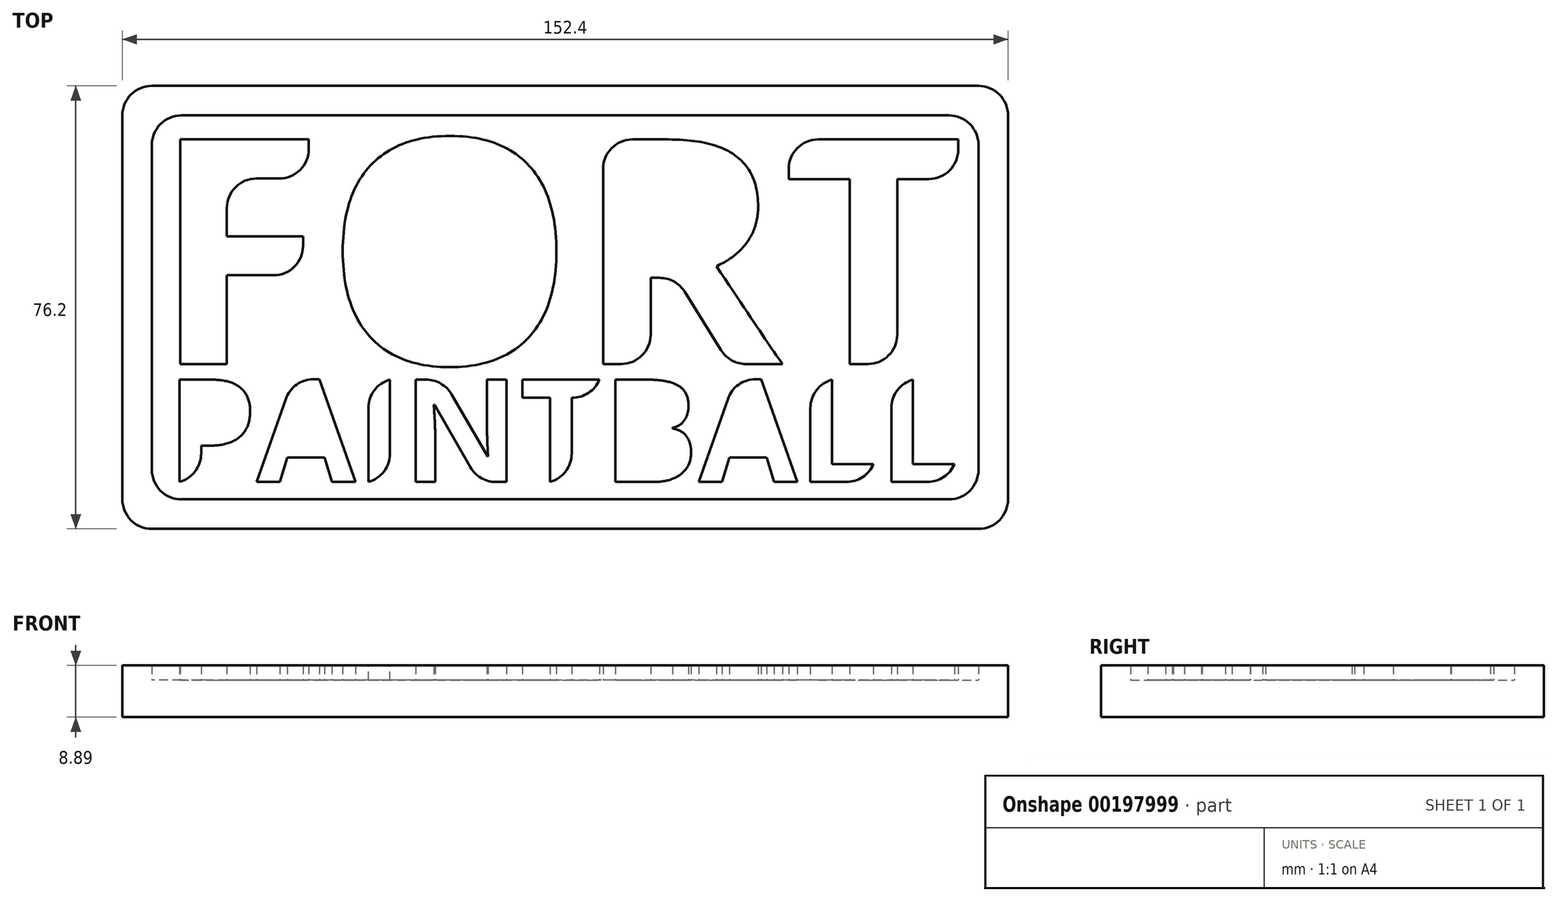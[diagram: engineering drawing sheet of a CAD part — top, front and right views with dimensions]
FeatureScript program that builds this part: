
annotation { "Feature Type Name" : "Feature", "Feature Type Description" : "" }
export const myFeature = defineFeature(function(context is Context, id is Id, definition is map)
    precondition{}
    {
        {
            var Q0;
            Q0=qCreatedBy(makeId("Top.planeOp"),FACE);
            var sketch = newSketch(context, id + "F0", { "sketchPlane" : qUnion([Q0])});
            skLineSegment(sketch, "E0.bottom", {"start": v(76.2, -38.1) * mm, "end": v(-76.2, -38.1) * mm});
            skLineSegment(sketch, "E0.top", {"start": v(76.2, 38.1) * mm, "end": v(-76.2, 38.1) * mm});
            skLineSegment(sketch, "E0.left", {"start": v(76.2, -38.1) * mm, "end": v(76.2, 38.1) * mm});
            skLineSegment(sketch, "E0.right", {"start": v(-76.2, -38.1) * mm, "end": v(-76.2, 38.1) * mm});
            skPoint(sketch, "E0.middle", {"position": v(0, 0) * mm});
            skText(sketch, "E1", { "text": "FORT", "fontName": "OpenSans-Bold.ttf"});
            skLineSegment(sketch, "E2.0", {"start": v(71.12, 33.02) * mm, "end": v(-71.12, 33.02) * mm});
            skLineSegment(sketch, "E2.1", {"start": v(71.12, -33.02) * mm, "end": v(71.12, 33.02) * mm});
            skLineSegment(sketch, "E2.2", {"start": v(71.12, -33.02) * mm, "end": v(-71.12, -33.02) * mm});
            skLineSegment(sketch, "E2.3", {"start": v(-71.12, -33.02) * mm, "end": v(-71.12, 33.02) * mm});
            skText(sketch, "E3", { "text": "PAINTBALL", "fontName": "OpenSans-Bold.ttf"});
            const initialGuessF0  = {"E1": [-0.07112, -0.00975, 1, 0, 0.03896], "E3": [-0.06858, -0.03004, 1, 0, 0.01775]};
            skSetInitialGuess(sketch, initialGuessF0);
            skSolve(sketch);
        }
        {
            var Q0;
            Q0=makeQuery(id+"F0.imprint","IMPRINT",FACE,{"disambiguationData":[TD([[makeQuery(id+"F0.imprint","IMPRINT",EDGE,{"derivedFrom":sQuery(id+"F0.wireOp",EDGE,"E1.sketch_text.stroke-0")}),1.0]])]});
            extrude(context, id + "F1", {"entities" : qUnion([Q0]), "depth" : 6.35 * mm});
        }
        {
            var Q0;
            Q0=makeQuery(id+"F0.imprint","IMPRINT",FACE,{"disambiguationData":[TD([[makeQuery(id+"F0.imprint","IMPRINT",EDGE,{"derivedFrom":sQuery(id+"F0.wireOp",EDGE,"E3.sketch_text.stroke-79")}),-1.0]])]});
            var Q1;
            Q1=makeQuery(id+"F0.imprint","IMPRINT",FACE,{"disambiguationData":[TD([[makeQuery(id+"F0.imprint","IMPRINT",EDGE,{"derivedFrom":sQuery(id+"F0.wireOp",EDGE,"E3.sketch_text.stroke-87")}),1.0]])]});
            var Q2;
            Q2=makeQuery(id+"F0.imprint","IMPRINT",FACE,{"disambiguationData":[TD([[makeQuery(id+"F0.imprint","IMPRINT",EDGE,{"derivedFrom":sQuery(id+"F0.wireOp",EDGE,"E3.sketch_text.stroke-91")}),-1.0]])]});
            var Q3;
            Q3=makeQuery(id+"F0.imprint","IMPRINT",FACE,{"disambiguationData":[TD([[makeQuery(id+"F0.imprint","IMPRINT",EDGE,{"derivedFrom":sQuery(id+"F0.wireOp",EDGE,"E3.sketch_text.stroke-97")}),-1.0]])]});
            var Q4;
            Q4=makeQuery(id+"F0.imprint","IMPRINT",FACE,{"disambiguationData":[TD([[makeQuery(id+"F0.imprint","IMPRINT",EDGE,{"derivedFrom":sQuery(id+"F0.wireOp",EDGE,"E1.sketch_text.stroke-43")}),-1.0]])]});
            var Q5;
            Q5=makeQuery(id+"F0.imprint","IMPRINT",FACE,{"disambiguationData":[TD([[makeQuery(id+"F0.imprint","IMPRINT",EDGE,{"derivedFrom":sQuery(id+"F0.wireOp",EDGE,"E1.sketch_text.stroke-24")}),1.0]])]});
            var Q6;
            Q6=makeQuery(id+"F0.imprint","IMPRINT",FACE,{"disambiguationData":[TD([[makeQuery(id+"F0.imprint","IMPRINT",EDGE,{"derivedFrom":sQuery(id+"F0.wireOp",EDGE,"E1.sketch_text.stroke-24")}),-1.0]])]});
            var Q7;
            Q7=makeQuery(id+"F0.imprint","IMPRINT",FACE,{"disambiguationData":[TD([[makeQuery(id+"F0.imprint","IMPRINT",EDGE,{"derivedFrom":sQuery(id+"F0.wireOp",EDGE,"E1.sketch_text.stroke-10")}),-1.0]])]});
            var Q8;
            Q8=makeQuery(id+"F0.imprint","IMPRINT",FACE,{"disambiguationData":[TD([[makeQuery(id+"F0.imprint","IMPRINT",EDGE,{"derivedFrom":sQuery(id+"F0.wireOp",EDGE,"E1.sketch_text.stroke-18")}),1.0]])]});
            var Q9;
            Q9=makeQuery(id+"F0.imprint","IMPRINT",FACE,{"disambiguationData":[TD([[makeQuery(id+"F0.imprint","IMPRINT",EDGE,{"derivedFrom":sQuery(id+"F0.wireOp",EDGE,"E1.sketch_text.stroke-0")}),-1.0]])]});
            var Q10;
            Q10=makeQuery(id+"F0.imprint","IMPRINT",FACE,{"disambiguationData":[TD([[makeQuery(id+"F0.imprint","IMPRINT",EDGE,{"derivedFrom":sQuery(id+"F0.wireOp",EDGE,"E3.sketch_text.stroke-0")}),1.0]])]});
            var Q11;
            Q11=makeQuery(id+"F0.imprint","IMPRINT",FACE,{"disambiguationData":[TD([[makeQuery(id+"F0.imprint","IMPRINT",EDGE,{"derivedFrom":sQuery(id+"F0.wireOp",EDGE,"E3.sketch_text.stroke-0")}),-1.0]])]});
            var Q12;
            Q12=makeQuery(id+"F0.imprint","IMPRINT",FACE,{"disambiguationData":[TD([[makeQuery(id+"F0.imprint","IMPRINT",EDGE,{"derivedFrom":sQuery(id+"F0.wireOp",EDGE,"E3.sketch_text.stroke-16")}),-1.0]])]});
            var Q13;
            Q13=makeQuery(id+"F0.imprint","IMPRINT",FACE,{"disambiguationData":[TD([[makeQuery(id+"F0.imprint","IMPRINT",EDGE,{"derivedFrom":sQuery(id+"F0.wireOp",EDGE,"E3.sketch_text.stroke-24")}),1.0]])]});
            var Q14;
            Q14=makeQuery(id+"F0.imprint","IMPRINT",FACE,{"disambiguationData":[TD([[makeQuery(id+"F0.imprint","IMPRINT",EDGE,{"derivedFrom":sQuery(id+"F0.wireOp",EDGE,"E3.sketch_text.stroke-28")}),-1.0]])]});
            var Q15;
            Q15=makeQuery(id+"F0.imprint","IMPRINT",FACE,{"disambiguationData":[TD([[makeQuery(id+"F0.imprint","IMPRINT",EDGE,{"derivedFrom":sQuery(id+"F0.wireOp",EDGE,"E3.sketch_text.stroke-32")}),-1.0]])]});
            var Q16;
            Q16=makeQuery(id+"F0.imprint","IMPRINT",FACE,{"disambiguationData":[TD([[makeQuery(id+"F0.imprint","IMPRINT",EDGE,{"derivedFrom":sQuery(id+"F0.wireOp",EDGE,"E3.sketch_text.stroke-46")}),-1.0]])]});
            var Q17;
            Q17=makeQuery(id+"F0.imprint","IMPRINT",FACE,{"disambiguationData":[TD([[makeQuery(id+"F0.imprint","IMPRINT",EDGE,{"derivedFrom":sQuery(id+"F0.wireOp",EDGE,"E3.sketch_text.stroke-66")}),1.0]])]});
            var Q18;
            Q18=makeQuery(id+"F0.imprint","IMPRINT",FACE,{"disambiguationData":[TD([[makeQuery(id+"F0.imprint","IMPRINT",EDGE,{"derivedFrom":sQuery(id+"F0.wireOp",EDGE,"E3.sketch_text.stroke-54")}),-1.0]])]});
            var Q19;
            Q19=makeQuery(id+"F0.imprint","IMPRINT",FACE,{"disambiguationData":[TD([[makeQuery(id+"F0.imprint","IMPRINT",EDGE,{"derivedFrom":sQuery(id+"F0.wireOp",EDGE,"E3.sketch_text.stroke-73")}),1.0]])]});
            var Q20;
            Q20=makeQuery(id+"F0.imprint","IMPRINT",FACE,{"disambiguationData":[TD([[makeQuery(id+"F0.imprint","IMPRINT",EDGE,{"derivedFrom":sQuery(id+"F0.wireOp",EDGE,"E0.bottom")}),-1.0]])]});
            extrude(context, id + "F2", {"entities" : qUnion([Q0, Q1, Q2, Q3, Q4, Q5, Q6, Q7, Q8, Q9, Q10, Q11, Q12, Q13, Q14, Q15, Q16, Q17, Q18, Q19, Q20]), "operationType" : NewBodyOperationType.ADD, "depth" : 8.9 * mm});
        }
        {
            var Q0;
            Q0=makeQuery(id+"F2.opExtrude","SWEPT_EDGE",EDGE,{"disambiguationData":[OSD([sQuery(id+"F0.wireOp",EDGE,"E1.sketch_text.stroke-43"),sQuery(id+"F0.wireOp",EDGE,"E1.sketch_text.stroke-50")])]});
            var Q1;
            Q1=makeQuery(id+"F2.opExtrude","SWEPT_EDGE",EDGE,{"disambiguationData":[OSD([sQuery(id+"F0.wireOp",EDGE,"E1.sketch_text.stroke-46"),sQuery(id+"F0.wireOp",EDGE,"E1.sketch_text.stroke-47")])]});
            var Q2;
            Q2=makeQuery(id+"F2.opExtrude","SWEPT_EDGE",EDGE,{"disambiguationData":[OSD([sQuery(id+"F0.wireOp",EDGE,"E1.sketch_text.stroke-48"),sQuery(id+"F0.wireOp",EDGE,"E1.sketch_text.stroke-49")])]});
            var Q3;
            Q3=makeQuery(id+"F2.opExtrude","SWEPT_EDGE",EDGE,{"disambiguationData":[OSD([sQuery(id+"F0.wireOp",EDGE,"E1.sketch_text.stroke-33"),sQuery(id+"F0.wireOp",EDGE,"E1.sketch_text.stroke-34")])]});
            var Q4;
            Q4=makeQuery(id+"F2.opExtrude","SWEPT_EDGE",EDGE,{"disambiguationData":[OSD([sQuery(id+"F0.wireOp",EDGE,"E1.sketch_text.stroke-40"),sQuery(id+"F0.wireOp",EDGE,"E1.sketch_text.stroke-41")])]});
            var Q5;
            Q5=makeQuery(id+"F2.opExtrude","SWEPT_EDGE",EDGE,{"disambiguationData":[OSD([sQuery(id+"F0.wireOp",EDGE,"E1.sketch_text.stroke-31"),sQuery(id+"F0.wireOp",EDGE,"E1.sketch_text.stroke-32")])]});
            var Q6;
            Q6=makeQuery(id+"F2.opExtrude","SWEPT_EDGE",EDGE,{"disambiguationData":[OSD([sQuery(id+"F0.wireOp",EDGE,"E1.sketch_text.stroke-3"),sQuery(id+"F0.wireOp",EDGE,"E1.sketch_text.stroke-4")])]});
            var Q7;
            Q7=makeQuery(id+"F2.opExtrude","SWEPT_EDGE",EDGE,{"disambiguationData":[OSD([sQuery(id+"F0.wireOp",EDGE,"E1.sketch_text.stroke-7"),sQuery(id+"F0.wireOp",EDGE,"E1.sketch_text.stroke-8")])]});
            var Q8;
            Q8=makeQuery(id+"F2.opExtrude","SWEPT_EDGE",EDGE,{"disambiguationData":[OSD([sQuery(id+"F0.wireOp",EDGE,"E3.sketch_text.stroke-20"),sQuery(id+"F0.wireOp",EDGE,"E3.sketch_text.stroke-21")])]});
            var Q9;
            Q9=makeQuery(id+"F2.opExtrude","SWEPT_EDGE",EDGE,{"disambiguationData":[OSD([sQuery(id+"F0.wireOp",EDGE,"E3.sketch_text.stroke-28"),sQuery(id+"F0.wireOp",EDGE,"E3.sketch_text.stroke-29")])]});
            var Q10;
            Q10=makeQuery(id+"F2.opExtrude","SWEPT_EDGE",EDGE,{"disambiguationData":[OSD([sQuery(id+"F0.wireOp",EDGE,"E3.sketch_text.stroke-30"),sQuery(id+"F0.wireOp",EDGE,"E3.sketch_text.stroke-31")])]});
            var Q11;
            Q11=makeQuery(id+"F2.opExtrude","SWEPT_EDGE",EDGE,{"disambiguationData":[OSD([sQuery(id+"F0.wireOp",EDGE,"E3.sketch_text.stroke-51"),sQuery(id+"F0.wireOp",EDGE,"E3.sketch_text.stroke-52")])]});
            var Q12;
            Q12=makeQuery(id+"F2.opExtrude","SWEPT_EDGE",EDGE,{"disambiguationData":[OSD([sQuery(id+"F0.wireOp",EDGE,"E3.sketch_text.stroke-46"),sQuery(id+"F0.wireOp",EDGE,"E3.sketch_text.stroke-53")])]});
            var Q13;
            Q13=makeQuery(id+"F2.opExtrude","SWEPT_EDGE",EDGE,{"disambiguationData":[OSD([sQuery(id+"F0.wireOp",EDGE,"E3.sketch_text.stroke-32"),sQuery(id+"F0.wireOp",EDGE,"E3.sketch_text.stroke-33")])]});
            var Q14;
            Q14=makeQuery(id+"F2.opExtrude","SWEPT_EDGE",EDGE,{"disambiguationData":[OSD([sQuery(id+"F0.wireOp",EDGE,"E3.sketch_text.stroke-39"),sQuery(id+"F0.wireOp",EDGE,"E3.sketch_text.stroke-40")])]});
            var Q15;
            Q15=makeQuery(id+"F2.opExtrude","SWEPT_EDGE",EDGE,{"disambiguationData":[OSD([sQuery(id+"F0.wireOp",EDGE,"E3.sketch_text.stroke-95"),sQuery(id+"F0.wireOp",EDGE,"E3.sketch_text.stroke-96")])]});
            var Q16;
            Q16=makeQuery(id+"F2.opExtrude","SWEPT_EDGE",EDGE,{"disambiguationData":[OSD([sQuery(id+"F0.wireOp",EDGE,"E3.sketch_text.stroke-101"),sQuery(id+"F0.wireOp",EDGE,"E3.sketch_text.stroke-102")])]});
            var Q17;
            Q17=makeQuery(id+"F2.opExtrude","SWEPT_EDGE",EDGE,{"disambiguationData":[OSD([sQuery(id+"F0.wireOp",EDGE,"E3.sketch_text.stroke-91"),sQuery(id+"F0.wireOp",EDGE,"E3.sketch_text.stroke-92")])]});
            var Q18;
            Q18=makeQuery(id+"F2.opExtrude","SWEPT_EDGE",EDGE,{"disambiguationData":[OSD([sQuery(id+"F0.wireOp",EDGE,"E3.sketch_text.stroke-97"),sQuery(id+"F0.wireOp",EDGE,"E3.sketch_text.stroke-98")])]});
            var Q19;
            Q19=makeQuery(id+"F2.opExtrude","SWEPT_EDGE",EDGE,{"disambiguationData":[OSD([sQuery(id+"F0.wireOp",EDGE,"E3.sketch_text.stroke-83"),sQuery(id+"F0.wireOp",EDGE,"E3.sketch_text.stroke-84")])]});
            var Q20;
            Q20=makeQuery(id+"F2.opExtrude","SWEPT_EDGE",EDGE,{"disambiguationData":[OSD([sQuery(id+"F0.wireOp",EDGE,"E3.sketch_text.stroke-10"),sQuery(id+"F0.wireOp",EDGE,"E3.sketch_text.stroke-11")])]});
            var Q21;
            Q21=makeQuery(id+"F2.opExtrude","SWEPT_EDGE",EDGE,{"disambiguationData":[OSD([sQuery(id+"F0.wireOp",EDGE,"E1.sketch_text.stroke-4"),sQuery(id+"F0.wireOp",EDGE,"E1.sketch_text.stroke-5")])]});
            var Q22;
            Q22=makeQuery(id+"F2.opExtrude","SWEPT_EDGE",EDGE,{"disambiguationData":[OSD([sQuery(id+"F0.wireOp",EDGE,"E1.sketch_text.stroke-41"),sQuery(id+"F0.wireOp",EDGE,"E1.sketch_text.stroke-42")])]});
            var Q23;
            Q23=makeQuery(id+"F2.opExtrude","SWEPT_EDGE",EDGE,{"disambiguationData":[OSD([sQuery(id+"F0.wireOp",EDGE,"E0.bottom"),sQuery(id+"F0.wireOp",EDGE,"E0.right")])]});
            var Q24;
            Q24=makeQuery(id+"F2.opExtrude","SWEPT_EDGE",EDGE,{"disambiguationData":[OSD([sQuery(id+"F0.wireOp",EDGE,"E0.top"),sQuery(id+"F0.wireOp",EDGE,"E0.right")])]});
            var Q25;
            Q25=makeQuery(id+"F2.opExtrude","SWEPT_EDGE",EDGE,{"disambiguationData":[OSD([sQuery(id+"F0.wireOp",EDGE,"E0.bottom"),sQuery(id+"F0.wireOp",EDGE,"E0.left")])]});
            var Q26;
            Q26=makeQuery(id+"F2.opExtrude","SWEPT_EDGE",EDGE,{"disambiguationData":[OSD([sQuery(id+"F0.wireOp",EDGE,"E0.top"),sQuery(id+"F0.wireOp",EDGE,"E0.left")])]});
            var Q27;
            Q27=makeQuery(id+"F2.opExtrude","SWEPT_EDGE",EDGE,{"disambiguationData":[OSD([sQuery(id+"F0.wireOp",EDGE,"E2.2"),sQuery(id+"F0.wireOp",EDGE,"E2.3")])]});
            var Q28;
            Q28=makeQuery(id+"F2.opExtrude","SWEPT_EDGE",EDGE,{"disambiguationData":[OSD([sQuery(id+"F0.wireOp",EDGE,"E2.0"),sQuery(id+"F0.wireOp",EDGE,"E2.1")])]});
            var Q29;
            Q29=makeQuery(id+"F2.opExtrude","SWEPT_EDGE",EDGE,{"disambiguationData":[OSD([sQuery(id+"F0.wireOp",EDGE,"E2.0"),sQuery(id+"F0.wireOp",EDGE,"E2.3")])]});
            var Q30;
            Q30=makeQuery(id+"F2.opExtrude","SWEPT_EDGE",EDGE,{"disambiguationData":[OSD([sQuery(id+"F0.wireOp",EDGE,"E2.1"),sQuery(id+"F0.wireOp",EDGE,"E2.2")])]});
            fillet(context, id + "F3", {"entities" : qUnion([Q0, Q1, Q2, Q3, Q4, Q5, Q6, Q7, Q8, Q9, Q10, Q11, Q12, Q13, Q14, Q15, Q16, Q17, Q18, Q19, Q20, Q21, Q22, Q23, Q24, Q25, Q26, Q27, Q28, Q29, Q30]), "radius" : 5.08 * mm, "tangentPropagation" : true, "allowEdgeOverflow" : false});
        }
    });
